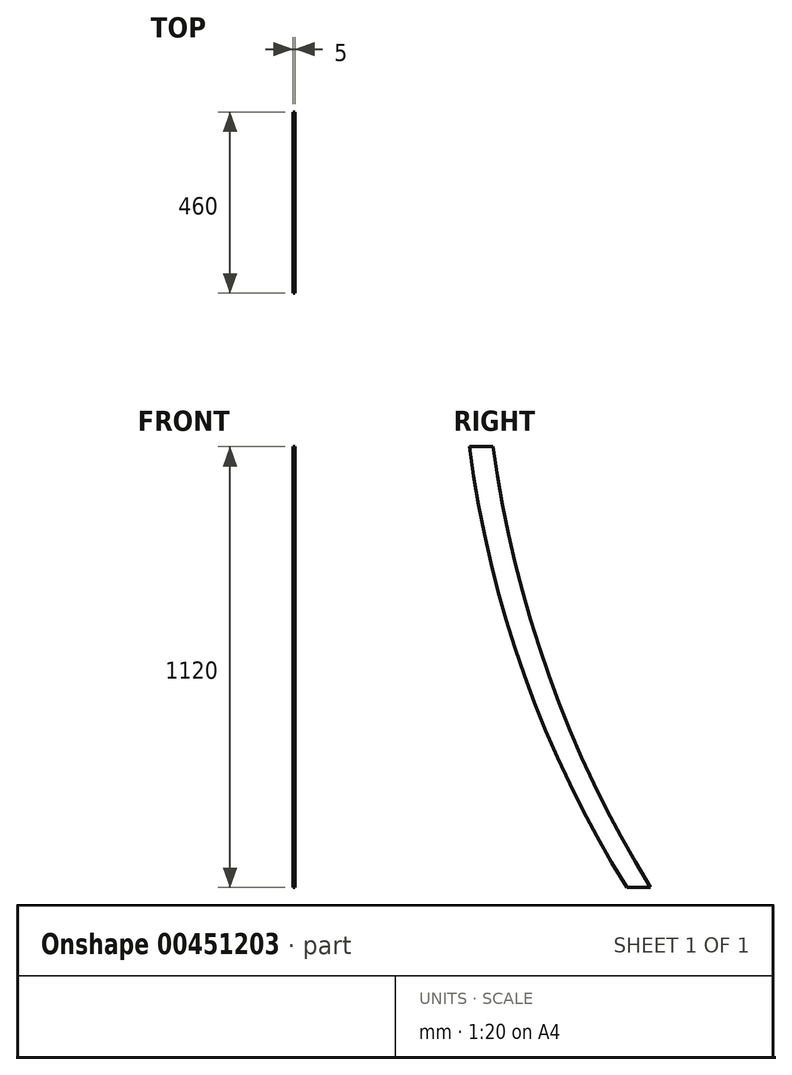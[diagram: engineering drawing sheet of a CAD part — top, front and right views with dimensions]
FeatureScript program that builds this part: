
annotation { "Feature Type Name" : "Feature", "Feature Type Description" : "" }
export const myFeature = defineFeature(function(context is Context, id is Id, definition is map)
    precondition{}
    {
        {
            var Q0;
            Q0=qCreatedBy(makeId("Right.planeOp"),FACE);
            var sketch = newSketch(context, id + "F0", { "sketchPlane" : qUnion([Q0])});
            skLineSegment(sketch, "E0", {"start": v(0, 0) * mm, "end": v(-60, 0) * mm});
            skLineSegment(sketch, "E1", {"start": v(-460, 1120) * mm, "end": v(-400, 1120) * mm});
            skArc(sketch, "E2", {"start": v(-460, 1120) * mm, "mid": v(-320.56, 538.37) * mm, "end": v(-60, 0) * mm});
            skArc(sketch, "E3", {"start": v(-400, 1120) * mm, "mid": v(-258.78, 539) * mm, "end": v(0, 0) * mm});
            skSolve(sketch);
        }
        {
            var Q0;
            Q0 = qSketchRegion(id + "F0", true);
            extrude(context, id + "F1", {"entities" : qUnion([Q0]), "depth" : 5 * mm, "offsetDistance" : 25 * mm});
        }
    });
